# Revit family: GD10 3000-4000 Shelf
name_source: partatom
category: Furniture
units: mm (PartAtom-declared; Revit-internal decimal feet)

## family parameters
Always vertical = Yes
Cut with Voids When Loaded = No
OmniClass Number = 23.40.20.00
OmniClass Title = General Furniture and Specialties
Room Calculation Point = No
Shared = No
Work Plane-Based = No

## types (2) — shared parameters
Assembly Code = E2020200
Depth = 900 mm  [stored 2.95276 ft]
Frame = Gresham - SOLID OAK
Height = 742 mm  [stored 2.43438 ft]
Light = Gresham -LIGHT
Manufacturer = Gresham Office Furniture
Range = GD10
URL = www.gof.co.uk

## per-type parameters (varying)
| type | Width |
| 3000 Light | 3000 mm  [stored 9.84252 ft] |
| 4000 Light | 4000 mm  [stored 13.1234 ft] |

note: column(s) folded — value = type name in every type: Product Code

note: [stored X ft] marks values corroborated as IEEE doubles in the binary element streams (Revit-internal decimal feet)

## geometry (parser evidence)
native form markers: Sweep x2
no freeform markers — native parametric forms only
